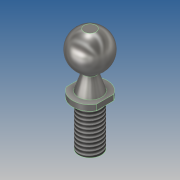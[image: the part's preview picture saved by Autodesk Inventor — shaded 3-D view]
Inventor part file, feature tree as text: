
AUTODESK INVENTOR PART (.ipt)
format: ipt  version: 2018.2 (Build 222227000, 227)  size: 139,776 bytes
history: native  units: in
note: dims shown in document units (in); Inventor stores cm internally (conversion verified against a paired STEP export)
features: thread x1
ambient origin geometry x8: Origin, YZ Plane, XZ Plane, XY Plane, X Axis, Y Axis, Z Axis, Center Point
bodies: Volumenkörper1 (feature_tree)
feature tree (1):
  thread  "Gewinde1"  [1 undecoded]
note: 1 required parameter value undecoded (feature->parameter linkage not recoverable at this tier; creation-order binding heuristic only, values carry confidence <= 0.55)
